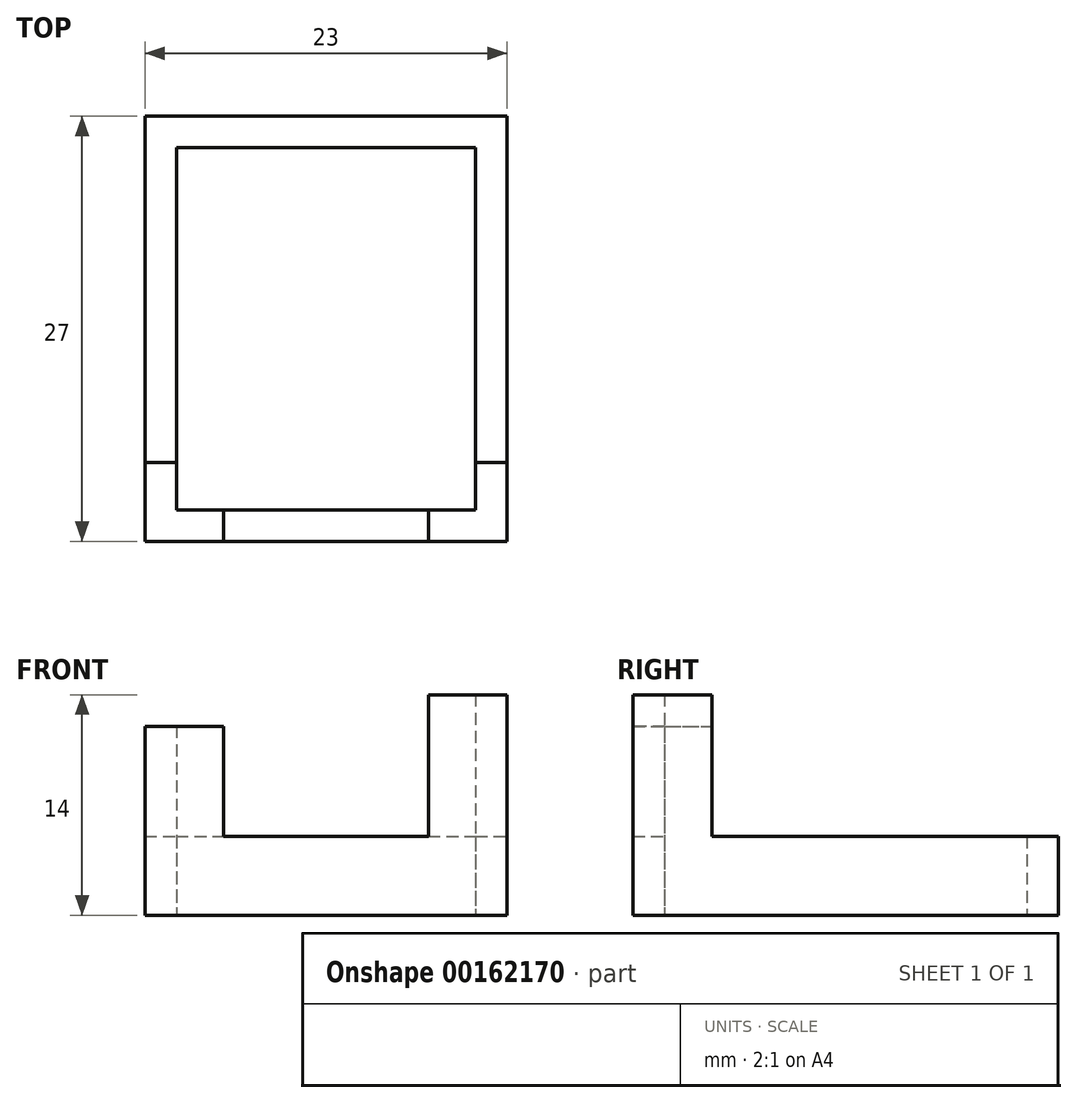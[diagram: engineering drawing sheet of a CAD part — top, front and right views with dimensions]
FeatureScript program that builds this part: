
annotation { "Feature Type Name" : "Feature", "Feature Type Description" : "" }
export const myFeature = defineFeature(function(context is Context, id is Id, definition is map)
    precondition{}
    {
        {
            var Q0;
            Q0=qCreatedBy(makeId("Top.planeOp"),FACE);
            var sketch = newSketch(context, id + "F0", { "sketchPlane" : qUnion([Q0])});
            skLineSegment(sketch, "E0", {"start": v(0, 0) * mm, "end": v(0, 23) * mm});
            skLineSegment(sketch, "E1", {"start": v(0, 0) * mm, "end": v(19, 0) * mm});
            skLineSegment(sketch, "E2", {"start": v(21, -2) * mm, "end": v(-2, -2) * mm});
            skLineSegment(sketch, "E3", {"start": v(19, 0) * mm, "end": v(19, 23) * mm});
            skLineSegment(sketch, "E4", {"start": v(0, 23) * mm, "end": v(19, 23) * mm});
            skLineSegment(sketch, "E5", {"start": v(-2, 25) * mm, "end": v(21, 25) * mm});
            skLineSegment(sketch, "E6", {"start": v(-2, -2) * mm, "end": v(-2, 25) * mm});
            skLineSegment(sketch, "E7", {"start": v(21, -2) * mm, "end": v(21, 25) * mm});
            skSolve(sketch);
        }
        {
            var Q0;
            Q0 = qSketchRegion(id + "F0", true);
            extrude(context, id + "F1", {"entities" : qUnion([Q0]), "depth" : 5 * mm});
        }
        {
            var Q0;
            Q0=makeQuery(id+"F1.opExtrude","CAP_FACE",FACE,{"disambiguationData":[OSD([sQuery(id+"F0.wireOp",EDGE,"E0"),sQuery(id+"F0.wireOp",EDGE,"fMDAZUCE-WxNw-tCVg-Pr7f-gKTRDs7ux1xq"),sQuery(id+"F0.wireOp",EDGE,"E1"),sQuery(id+"F0.wireOp",EDGE,"E2"),sQuery(id+"F0.wireOp",EDGE,"em9QBzyh-X0cC-lrsQ-LOUW-UWbV2uQWN0fi"),sQuery(id+"F0.wireOp",EDGE,"E3"),sQuery(id+"F0.wireOp",EDGE,"HnKAWu8F-w6AE-VERm-Axyq-VS4Tu44atyqC"),sQuery(id+"F0.wireOp",EDGE,"QTcbnend-T0hK-HJJc-kWl9-1F0Q0khNvwRf")])],"isStart":false});
            var sketch = newSketch(context, id + "F2", { "sketchPlane" : qUnion([Q0])});
            skLineSegment(sketch, "E8", {"start": v(0, 0) * mm, "end": v(3, 0) * mm});
            skLineSegment(sketch, "E9", {"start": v(3, 0) * mm, "end": v(3, -2) * mm});
            skLineSegment(sketch, "E10", {"start": v(3, -2) * mm, "end": v(-2, -2) * mm});
            skLineSegment(sketch, "E11", {"start": v(-2, -2) * mm, "end": v(-2, 3) * mm});
            skLineSegment(sketch, "E12", {"start": v(-2, 3) * mm, "end": v(0, 3) * mm});
            skLineSegment(sketch, "E13", {"start": v(0, 3) * mm, "end": v(0, 0) * mm});
            skSolve(sketch);
        }
        {
            var Q0;
            Q0=makeQuery(id+"F2.imprint","IMPRINT",FACE,{"disambiguationData":[TD([[makeQuery(id+"F2.imprint","IMPRINT",EDGE,{"derivedFrom":sQuery(id+"F2.wireOp",EDGE,"E8")}),-1.0]])]});
            extrude(context, id + "F3", {"entities" : qUnion([Q0]), "operationType" : NewBodyOperationType.ADD, "depth" : 7 * mm});
        }
        {
            var Q0;
            {var subQ0=sQuery(id+"F0.wireOp",EDGE,"HnKAWu8F-w6AE-VERm-Axyq-VS4Tu44atyqC");var subQ1=sQuery(id+"F0.wireOp",EDGE,"E3");var subQ2=sQuery(id+"F0.wireOp",EDGE,"E2");var subQ3=sQuery(id+"F0.wireOp",EDGE,"E1");var subQ4=sQuery(id+"F0.wireOp",EDGE,"QTcbnend-T0hK-HJJc-kWl9-1F0Q0khNvwRf");Q0=makeQuery(id+"F3.boolean.opBoolean","SPLIT",FACE,{"disambiguationData":[TD([makeQuery(id+"F1.opExtrude","SWEPT_FACE",FACE,{"disambiguationData":[OSD([subQ3])]})])],"derivedFrom":makeQuery(id+"F1.opExtrude","CAP_FACE",FACE,{"disambiguationData":[OSD([sQuery(id+"F0.wireOp",EDGE,"E0"),sQuery(id+"F0.wireOp",EDGE,"fMDAZUCE-WxNw-tCVg-Pr7f-gKTRDs7ux1xq"),subQ3,subQ2,sQuery(id+"F0.wireOp",EDGE,"em9QBzyh-X0cC-lrsQ-LOUW-UWbV2uQWN0fi"),subQ1,subQ0,subQ4])],"isStart":false})});}
            var sketch = newSketch(context, id + "F4", { "sketchPlane" : qUnion([Q0])});
            skLineSegment(sketch, "E14", {"start": v(19, 0) * mm, "end": v(19, 3) * mm});
            skLineSegment(sketch, "E15", {"start": v(19, 3) * mm, "end": v(21, 3) * mm});
            skLineSegment(sketch, "E16", {"start": v(21, 3) * mm, "end": v(21, -2) * mm});
            skLineSegment(sketch, "E17", {"start": v(21, -2) * mm, "end": v(16, -2) * mm});
            skLineSegment(sketch, "E18", {"start": v(16, -2) * mm, "end": v(16, 0) * mm});
            skLineSegment(sketch, "E19", {"start": v(16, 0) * mm, "end": v(19, 0) * mm});
            skSolve(sketch);
        }
        {
            var Q0;
            Q0=makeQuery(id+"F4.imprint","IMPRINT",FACE,{"disambiguationData":[TD([[makeQuery(id+"F4.imprint","IMPRINT",EDGE,{"derivedFrom":sQuery(id+"F4.wireOp",EDGE,"E14")}),-1.0]])]});
            extrude(context, id + "F5", {"entities" : qUnion([Q0]), "operationType" : NewBodyOperationType.ADD, "depth" : 9 * mm});
        }
    });
